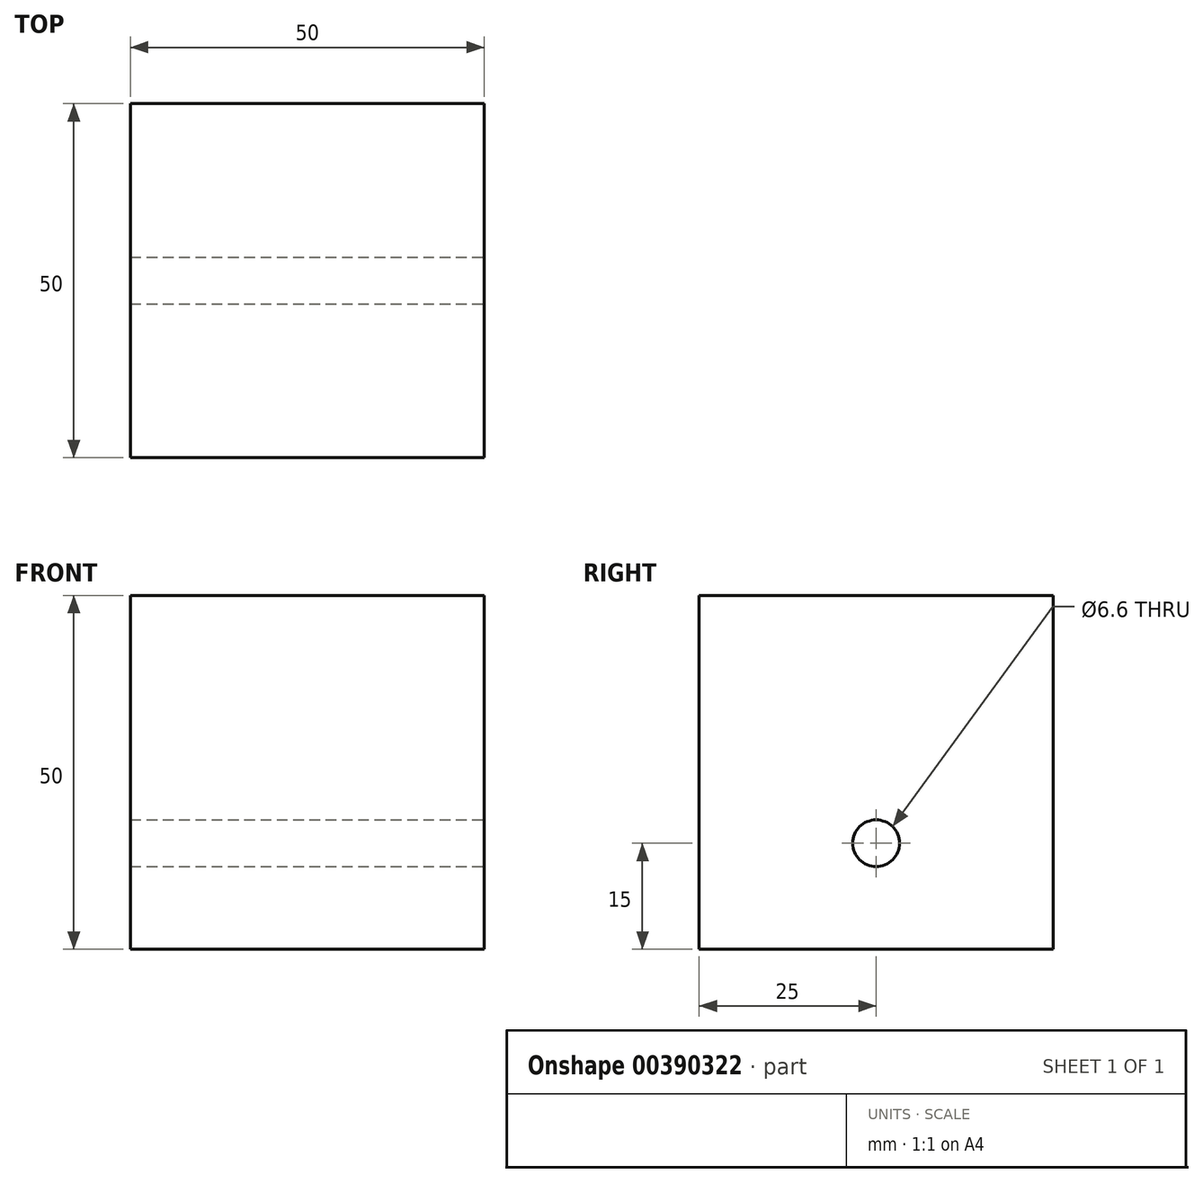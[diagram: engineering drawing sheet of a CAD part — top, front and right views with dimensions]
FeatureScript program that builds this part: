
annotation { "Feature Type Name" : "Feature", "Feature Type Description" : "" }
export const myFeature = defineFeature(function(context is Context, id is Id, definition is map)
    precondition{}
    {
        {
            var Q0;
            Q0=qCreatedBy(makeId("Front.planeOp"),FACE);
            var sketch = newSketch(context, id + "F0", { "sketchPlane" : qUnion([Q0])});
            skLineSegment(sketch, "E0.bottom", {"start": v(0, 0) * mm, "end": v(50, 0) * mm});
            skLineSegment(sketch, "E0.top", {"start": v(0, 50) * mm, "end": v(50, 50) * mm});
            skLineSegment(sketch, "E0.left", {"start": v(0, 0) * mm, "end": v(0, 50) * mm});
            skLineSegment(sketch, "E0.right", {"start": v(50, 0) * mm, "end": v(50, 50) * mm});
            skSolve(sketch);
        }
        {
            var Q0;
            Q0 = qSketchRegion(id + "F0", true);
            extrude(context, id + "F1", {"entities" : qUnion([Q0]), "depth" : 50 * mm});
        }
        {
            var Q0;
            Q0=makeQuery(id+"F1.opExtrude","SWEPT_FACE",FACE,{"disambiguationData":[OSD([sQuery(id+"F0.wireOp",EDGE,"E0.right")])]});
            var sketch = newSketch(context, id + "F2", { "sketchPlane" : qUnion([Q0])});
            skPoint(sketch, "E1", {"position": v(-25, 15) * mm});
            skSolve(sketch);
        }
        {
            var Q0;
            Q0=sQuery(id+"F2.wireOp",VERTEX,"E1");
            var Q1;
            Q1=makeQuery(id+"F1.opExtrude","SWEPT_BODY",BODY,{"disambiguationData":[OSD([sQuery(id+"F0.wireOp",EDGE,"E0.bottom"),sQuery(id+"F0.wireOp",EDGE,"E0.top"),sQuery(id+"F0.wireOp",EDGE,"E0.left"),sQuery(id+"F0.wireOp",EDGE,"E0.right")])]});
            hole(context, id + "F3", {"style" : HoleStyle.SIMPLE, "endStyle" : HoleEndStyle.THROUGH, "holeDiameter" : 6.6 * mm, "isTappedThrough" : true, "tappedDepth" : 22 * mm, "tapClearance" : 3, "locations" : qUnion([Q0]), "scope" : qUnion([Q1])});
        }
    });
